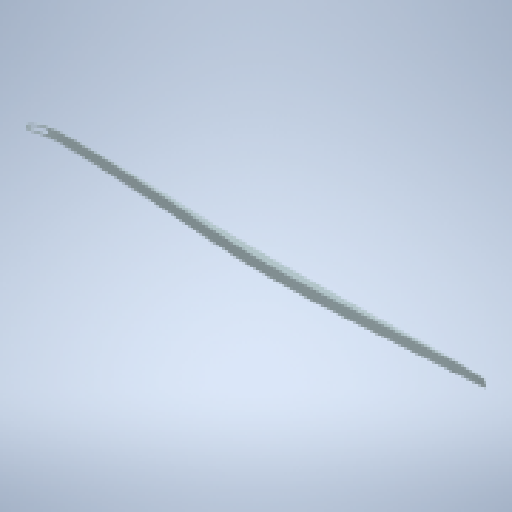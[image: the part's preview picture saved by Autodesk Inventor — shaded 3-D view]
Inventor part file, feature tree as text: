
AUTODESK INVENTOR PART (.ipt)
format: ipt  version: 2024 (Build 280153000, 153)  size: 904,192 bytes
history: native  units: in
note: dims shown in document units (in); Inventor stores cm internally (conversion verified against a paired STEP export)
features: plane x2, sketch x2, extrude x1
ambient origin geometry x8: Origin, YZ Plane, XZ Plane, XY Plane, X Axis, Y Axis, Z Axis, Center Point
bodies: Solid2 (feature_tree), Solid1 (feature_tree)
feature tree (5):
  plane  "Work Plane1"
  sketch  "Sketch1"  dims[d0=6.3125in d2=1.0236in]
  plane  "Work Plane2"
  extrude  "Extrusion1"  Depth=1.0236in
  sketch  "Sketch2"  dims[d3=6.0187in d4=0.0in d5=1.0236in d6=1.9685in]
